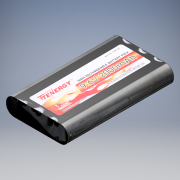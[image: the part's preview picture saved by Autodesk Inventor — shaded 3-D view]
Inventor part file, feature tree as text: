
AUTODESK INVENTOR PART (.ipt)
format: ipt  version: 2018 (Build 220112000, 112)  size: 766,976 bytes
history: native  units: in
note: dims shown in document units (in); Inventor stores cm internally (conversion verified against a paired STEP export)
features: other x12, sketch x7, projected_geometry x5, extrude x1, fillet x1
ambient origin geometry x8: Origin, YZ Plane, XZ Plane, XY Plane, X Axis, Y Axis, Z Axis, Center Point
bodies: Solid1 (feature_tree)
feature tree (26):
  extrude  "Extrusion1"  Depth=2.35in
  sketch  "Sketch2"  dims[d174=4.0in]
  sketch  "Sketch3"  dims[d175=0.65in]
  sketch  "Sketch4"  dims[d184=0.3in]
  sketch  "Sketch5"
  sketch  "Sketch6"
  sketch  "Sketch7"
  fillet  "Fillet2"  Radius=4.0in
  other  "Decal1"
  other  "Decal2"
  other  "Decal3"
  other  "Decal4"
  other  "Decal5"
  other  "Decal6"
  sketch  "Sketch1"  dims[d0=0.65in d1=2.35in d2=4.0in d3=0.0in]
  projected_geometry  "Projected Loop2"
  other  "Image5"
  projected_geometry  "Projected Loop3"
  other  "Image6"
  projected_geometry  "Projected Loop4"
  other  "Image8"
  projected_geometry  "Projected Loop5"
  other  "Image9"
  projected_geometry  "Projected Loop6"
  other  "Image10"
  other  "Image11"
